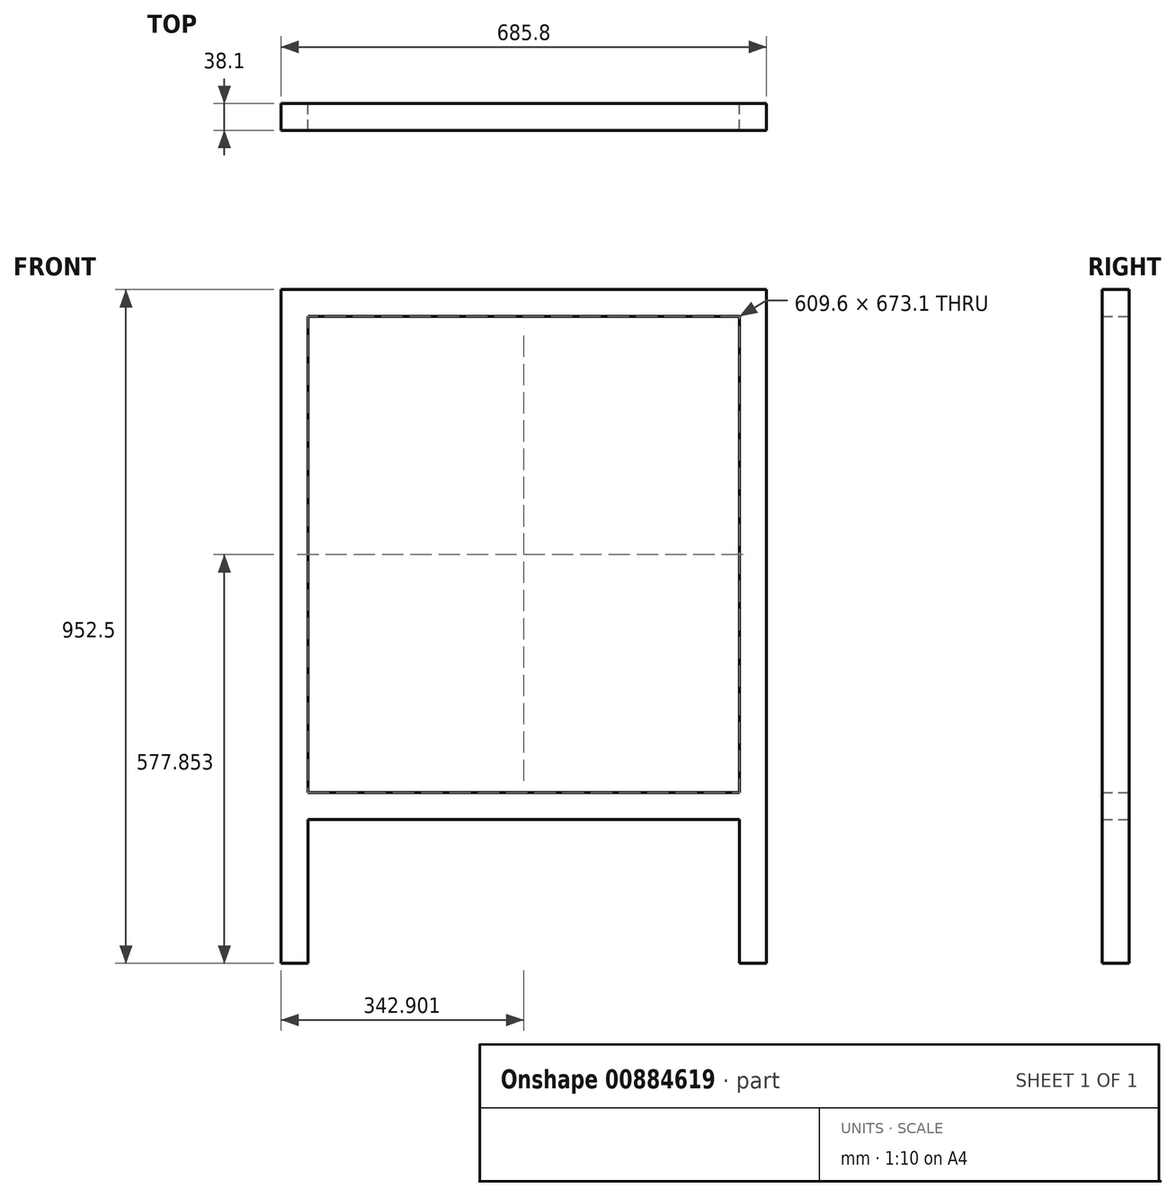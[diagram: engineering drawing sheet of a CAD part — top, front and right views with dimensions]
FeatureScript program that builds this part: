
annotation { "Feature Type Name" : "Feature", "Feature Type Description" : "" }
export const myFeature = defineFeature(function(context is Context, id is Id, definition is map)
    precondition{}
    {
        {
            var Q0;
            Q0=qCreatedBy(makeId("Front.planeOp"),FACE);
            var sketch = newSketch(context, id + "F0", { "sketchPlane" : qUnion([Q0])});
            skLineSegment(sketch, "E0.bottom", {"start": v(-577.75, -531.8) * mm, "end": v(-539.65, -531.8) * mm});
            skLineSegment(sketch, "E0.top", {"start": v(-577.75, 382.6) * mm, "end": v(-539.65, 382.6) * mm});
            skLineSegment(sketch, "E0.left", {"start": v(-577.75, -531.8) * mm, "end": v(-577.75, 382.6) * mm});
            skLineSegment(sketch, "E0.right", {"start": v(-539.65, -531.8) * mm, "end": v(-539.65, 382.6) * mm});
            skPoint(sketch, "E0.middle", {"position": v(-558.7, -74.6) * mm});
            skLineSegment(sketch, "E1.bottom", {"start": v(69.95, -531.8) * mm, "end": v(108.05, -531.8) * mm});
            skLineSegment(sketch, "E1.top", {"start": v(69.95, 382.6) * mm, "end": v(108.05, 382.6) * mm});
            skLineSegment(sketch, "E1.left", {"start": v(69.95, -531.8) * mm, "end": v(69.95, 382.6) * mm});
            skLineSegment(sketch, "E1.right", {"start": v(108.05, -531.8) * mm, "end": v(108.05, 382.6) * mm});
            skPoint(sketch, "E1.middle", {"position": v(89, -74.6) * mm});
            skLineSegment(sketch, "E2.bottom", {"start": v(-577.75, 382.6) * mm, "end": v(108.05, 382.6) * mm});
            skLineSegment(sketch, "E2.top", {"start": v(-577.75, 420.7) * mm, "end": v(108.05, 420.7) * mm});
            skLineSegment(sketch, "E2.left", {"start": v(-577.75, 382.6) * mm, "end": v(-577.75, 420.7) * mm});
            skLineSegment(sketch, "E2.right", {"start": v(108.05, 382.6) * mm, "end": v(108.05, 420.7) * mm});
            skLineSegment(sketch, "E3.bottom", {"start": v(-539.65, -328.6) * mm, "end": v(69.95, -328.6) * mm});
            skLineSegment(sketch, "E3.top", {"start": v(-539.65, -290.5) * mm, "end": v(69.95, -290.5) * mm});
            skLineSegment(sketch, "E3.left", {"start": v(-539.65, -328.6) * mm, "end": v(-539.65, -290.5) * mm});
            skLineSegment(sketch, "E3.right", {"start": v(69.95, -328.6) * mm, "end": v(69.95, -290.5) * mm});
            skSolve(sketch);
        }
        {
            var Q0;
            Q0=makeQuery(id+"F0.imprint","IMPRINT",FACE,{"disambiguationData":[TD([[makeQuery(id+"F0.imprint","IMPRINT",EDGE,{"derivedFrom":sQuery(id+"F0.wireOp",EDGE,"E2.top")}),-1.0]])]});
            var Q1;
            {var subQ4=sQuery(id+"F0.wireOp",EDGE,"E0.bottom");Q1=makeQuery(id+"F0.imprint","IMPRINT",FACE,{"disambiguationData":[TD([[makeQuery(id+"F0.imprint","IMPRINT",EDGE,{"derivedFrom":subQ4}),1.0]])]});}
            var Q2;
            {var subQ5=sQuery(id+"F0.wireOp",EDGE,"E1.bottom");Q2=makeQuery(id+"F0.imprint","IMPRINT",FACE,{"disambiguationData":[TD([[makeQuery(id+"F0.imprint","IMPRINT",EDGE,{"derivedFrom":subQ5}),1.0]])]});}
            var Q3;
            Q3=makeQuery(id+"F0.imprint","IMPRINT",FACE,{"disambiguationData":[TD([[makeQuery(id+"F0.imprint","IMPRINT",EDGE,{"derivedFrom":sQuery(id+"F0.wireOp",EDGE,"E3.bottom")}),1.0]])]});
            var Q4;
            Q4=sQuery(id+"F0.wireOp",EDGE,"E2.bottom");
            var Q5;
            Q5=sQuery(id+"F0.wireOp",EDGE,"E2.top");
            extrude(context, id + "F1", {"entities" : qUnion([Q0, Q1, Q2, Q3]), "surfaceEntities" : qUnion([Q4, Q5]), "depth" : 38.1 * mm, "offsetDistance" : 25.4 * mm});
        }
    });
